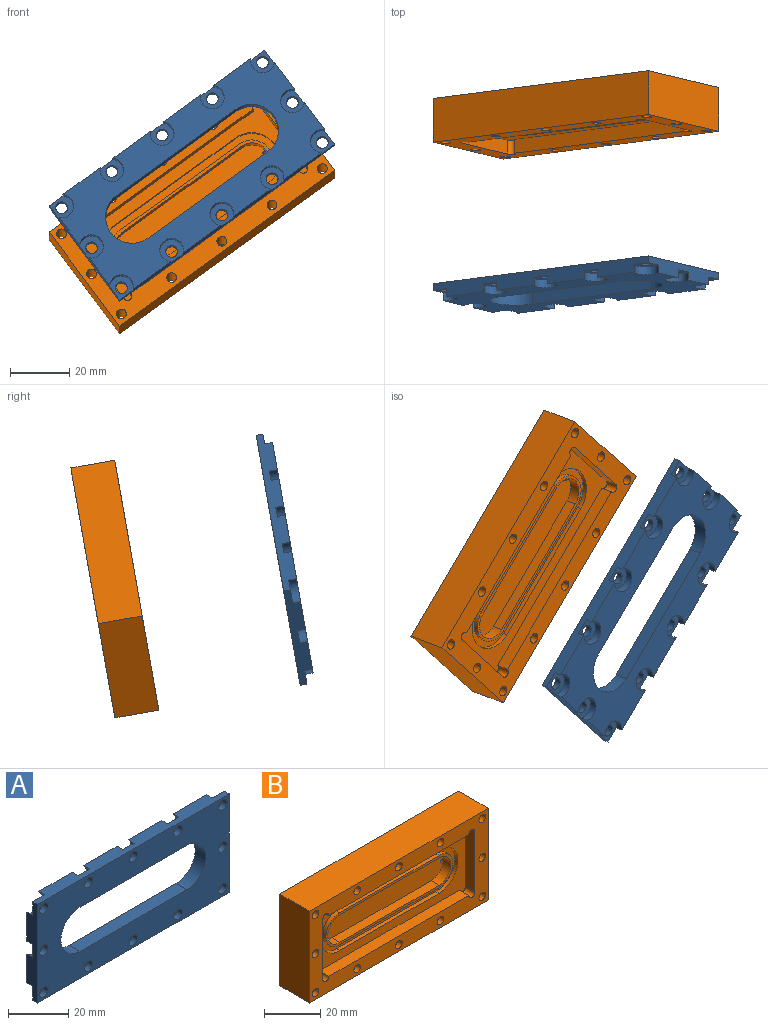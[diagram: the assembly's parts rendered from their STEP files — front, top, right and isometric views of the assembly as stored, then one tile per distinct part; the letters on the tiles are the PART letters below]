
ASSEMBLY  parts=2 mates=2
PART A: 46 faces, bbox 90x5x40 mm
  f0: plane 90x40mm, normal (0,1,0), area 1900.1mm2, adj f2,f3,f4,f17,f18,f20,f22,f24
  f1: plane 90x40mm, normal (0,-1,0), area 2294.7mm2, adj f2,f3,f4,f5,f6,f7,f8,f9
  f2: plane 40x5mm, normal (1,0,0), area 155.2mm2, adj f0,f1,f4,f17,f36,f37,f38,f39
  f3: plane 40x5mm, normal (-1,0,0), area 155.2mm2, adj f0,f1,f4,f17,f24,f25,f26,f27
  f4: plane 90x5mm, normal (0,0,-1), area 376.7mm2, adj f0,f1,f2,f3,f28,f29,f30,f31
  f5: cylinder r=2mm len=4mm, axis (0,1,0), area 28.9mm2, adj f1,f41
  f6: cylinder r=2mm len=4mm, axis (0,1,0), area 28.9mm2, adj f1,f39
  f7: cylinder r=2mm len=4mm, axis (0,1,0), area 28.9mm2, adj f1,f37
  f8: cylinder r=2mm len=4mm, axis (0,1,0), area 28.9mm2, adj f1,f35
  f9: cylinder r=2mm len=4mm, axis (0,1,0), area 28.9mm2, adj f1,f33
  f10: cylinder r=2mm len=4mm, axis (0,1,0), area 28.9mm2, adj f1,f31
  f11: cylinder r=2mm len=4mm, axis (0,1,0), area 28.9mm2, adj f1,f29
  f12: cylinder r=2mm len=4mm, axis (0,1,0), area 28.9mm2, adj f1,f27
  f13: cylinder r=2mm len=4mm, axis (0,1,0), area 28.9mm2, adj f1,f25
  f14: cylinder r=2mm len=4mm, axis (0,1,0), area 28.9mm2, adj f1,f23
  f15: cylinder r=2mm len=4mm, axis (0,1,0), area 28.9mm2, adj f1,f21
  f16: cylinder r=2mm len=4mm, axis (0,1,0), area 28.9mm2, adj f1,f19
  f17: plane 90x5mm, normal (0,0,1), area 376.7mm2, adj f0,f1,f2,f3,f18,f19,f20,f21
  f18: cylinder r=4mm len=8mm, axis (0,1,0), area 52.2mm2, adj f0,f17,f19
  f19: plane 8x7mm, normal (0,1,0), area 34.1mm2, adj f16,f17,f18
  f20: cylinder r=4mm len=8mm, axis (0,1,0), area 52.2mm2, adj f0,f17,f21
  f21: plane 8x7mm, normal (0,1,0), area 34.1mm2, adj f15,f17,f20
  f22: cylinder r=4mm len=8mm, axis (0,1,0), area 52.2mm2, adj f0,f17,f23
  f23: plane 8x7mm, normal (0,1,0), area 34.1mm2, adj f14,f17,f22
  f24: cylinder r=4mm len=7mm, axis (0,1,0), area 35.3mm2, adj f0,f3,f17,f25
  f25: plane 7x7mm, normal (0,1,0), area 30.5mm2, adj f3,f13,f17,f24
  f26: cylinder r=4mm len=8mm, axis (0,1,0), area 52.2mm2, adj f0,f3,f27
  f27: plane 8x7mm, normal (0,1,0), area 34.1mm2, adj f3,f12,f26
  f28: cylinder r=4mm len=7mm, axis (0,1,0), area 35.3mm2, adj f0,f3,f4,f29
  f29: plane 7x7mm, normal (0,1,0), area 30.5mm2, adj f3,f4,f11,f28
  f30: cylinder r=4mm len=8mm, axis (0,1,0), area 52.2mm2, adj f0,f4,f31
  f31: plane 8x7mm, normal (0,1,0), area 34.1mm2, adj f4,f10,f30
  f32: cylinder r=4mm len=8mm, axis (0,1,0), area 52.2mm2, adj f0,f4,f33
  f33: plane 8x7mm, normal (0,1,0), area 34.1mm2, adj f4,f9,f32
  f34: cylinder r=4mm len=8mm, axis (0,1,0), area 52.2mm2, adj f0,f4,f35
  f35: plane 8x7mm, normal (0,1,0), area 34.1mm2, adj f4,f8,f34
  f36: cylinder r=4mm len=7mm, axis (0,1,0), area 35.3mm2, adj f0,f2,f4,f37
  f37: plane 7x7mm, normal (0,1,0), area 30.5mm2, adj f2,f4,f7,f36
  f38: cylinder r=4mm len=8mm, axis (0,1,0), area 52.2mm2, adj f0,f2,f39
  f39: plane 8x7mm, normal (0,1,0), area 34.1mm2, adj f2,f6,f38
  f40: cylinder r=4mm len=7mm, axis (0,1,0), area 35.3mm2, adj f0,f2,f17,f41
  f41: plane 7x7mm, normal (0,1,0), area 30.5mm2, adj f2,f5,f17,f40
  f42: cylinder r=9mm len=18mm, axis (0,-1,0), area 141.4mm2, adj f0,f1,f43,f44
  f43: plane 50x5mm, normal (0,0,-1), area 250mm2, adj f0,f1,f42,f45
  f44: plane 50x5mm, normal (0,0,1), area 250mm2, adj f0,f1,f42,f45
  f45: cylinder r=9mm len=18mm, axis (0,-1,0), area 141.4mm2, adj f0,f1,f43,f44
PART B: 46 faces, bbox 90x15x40 mm
  f0: cylinder r=0.6mm len=5.74mm, axis (0,-1,0), area 21.6mm2, adj f4,f45
  f1: cylinder r=0.6mm len=5.74mm, axis (0,-1,0), area 21.6mm2, adj f4,f44
  f2: plane 90x40mm, normal (0,1,0), area 3489.8mm2, adj f7,f8,f9,f10,f32,f33,f34,f35
  f3: plane 90x40mm, normal (0,-1,0), area 1456mm2, adj f7,f8,f9,f10,f11,f12,f13,f14
  f4: plane 62x12mm, normal (0,-1,0), area 710.8mm2, adj f0,f1,f28,f29,f30,f31
  f5: plane 64x14mm, normal (0,-1,0), area 140.8mm2, adj f22,f23,f24,f25,f28,f29,f30,f31
  f6: plane 76.5x29.5mm, normal (0,-1,0), area 807.9mm2, adj f11,f12,f13,f14,f15,f16,f17,f18
  f7: plane 40x15mm, normal (1,0,0), area 600mm2, adj f2,f3,f8,f10
  f8: plane 90x15mm, normal (0,0,1), area 1350mm2, adj f2,f3,f7,f9
  f9: plane 40x15mm, normal (-1,0,0), area 600mm2, adj f2,f3,f8,f10
  f10: plane 90x15mm, normal (0,0,-1), area 1350mm2, adj f2,f3,f7,f9
  f11: cylinder r=1.5mm len=4.76mm, axis (0,-1,0), area 22.4mm2, adj f3,f6,f12,f18
  f12: plane 70.5x4.76mm, normal (0,0,-1), area 335.6mm2, adj f3,f6,f11,f13
  f13: cylinder r=1.5mm len=4.76mm, axis (0,-1,0), area 22.4mm2, adj f3,f6,f12,f14
  f14: plane 26.5x4.76mm, normal (1,0,0), area 126.1mm2, adj f3,f6,f13,f15
  f15: cylinder r=1.5mm len=4.76mm, axis (0,-1,0), area 22.4mm2, adj f3,f6,f14,f16
  f16: plane 70.5x4.76mm, normal (0,0,1), area 335.6mm2, adj f3,f6,f15,f17
  f17: cylinder r=1.5mm len=4.76mm, axis (0,-1,0), area 22.4mm2, adj f3,f6,f16,f18
  f18: plane 26.5x4.76mm, normal (-1,0,0), area 126.1mm2, adj f3,f6,f11,f17
  f19: plane 50x1.6mm, normal (0,0,-1), area 80mm2, adj f6,f20,f26,f27
  f20: cylinder r=9.5mm len=19mm, axis (0,-1,0), area 47.8mm2, adj f6,f19,f21,f27
  f21: plane 50x1.6mm, normal (0,0,1), area 80mm2, adj f6,f20,f26,f27
  f22: cylinder r=7mm len=14mm, axis (0,-1,0), area 35.2mm2, adj f5,f23,f25,f27
  f23: plane 50x1.6mm, normal (0,0,1), area 80mm2, adj f5,f22,f24,f27
  f24: cylinder r=7mm len=14mm, axis (0,-1,0), area 35.2mm2, adj f5,f23,f25,f27
  f25: plane 50x1.6mm, normal (0,0,-1), area 80mm2, adj f5,f22,f24,f27
  f26: cylinder r=9.5mm len=19mm, axis (0,-1,0), area 47.8mm2, adj f6,f19,f21,f27
  f27: plane 69x19mm, normal (0,-1,0), area 379.6mm2, adj f19,f20,f21,f22,f23,f24,f25,f26
  f28: plane 50x4mm, normal (0,0,-1), area 200mm2, adj f4,f5,f29,f31
  f29: cylinder r=6mm len=12mm, axis (0,-1,0), area 75.4mm2, adj f4,f5,f28,f30
  f30: plane 50x4mm, normal (0,0,1), area 200mm2, adj f4,f5,f29,f31
  f31: cylinder r=6mm len=12mm, axis (0,-1,0), area 75.4mm2, adj f4,f5,f28,f30
  f32: cylinder r=1.65mm len=15mm, axis (0,-1,0), area 155.5mm2, adj f2,f3
  f33: cylinder r=1.65mm len=15mm, axis (0,-1,0), area 155.5mm2, adj f2,f3
  f34: cylinder r=1.65mm len=15mm, axis (0,-1,0), area 155.5mm2, adj f2,f3
  f35: cylinder r=1.65mm len=15mm, axis (0,-1,0), area 155.5mm2, adj f2,f3
  f36: cylinder r=1.65mm len=15mm, axis (0,-1,0), area 155.5mm2, adj f2,f3
  f37: cylinder r=1.65mm len=15mm, axis (0,-1,0), area 155.5mm2, adj f2,f3
  f38: cylinder r=1.65mm len=15mm, axis (0,-1,0), area 155.5mm2, adj f2,f3
  f39: cylinder r=1.65mm len=15mm, axis (0,-1,0), area 155.5mm2, adj f2,f3
  f40: cylinder r=1.65mm len=15mm, axis (0,-1,0), area 155.5mm2, adj f2,f3
  f41: cylinder r=1.65mm len=15mm, axis (0,-1,0), area 155.5mm2, adj f2,f3
  f42: cylinder r=1.65mm len=15mm, axis (0,-1,0), area 155.5mm2, adj f2,f3
  f43: cylinder r=1.65mm len=15mm, axis (0,-1,0), area 155.5mm2, adj f2,f3
  f44: cone r=0.6mm half-angle=45deg, axis (0,1,0), area 3.8mm2, adj f1,f2
  f45: cone r=0.6mm half-angle=45deg, axis (0,1,0), area 3.8mm2, adj f0,f2
PLACE A rot(axis=(0.95,0.03,0.31),170.5deg) t=(-25.06,-84.72,-33.18)mm
PLACE B rot(axis=(-0.03,1,-0.09),143.8deg) t=(-25.06,-32.13,-42.45)mm
MATE planar A.f4 <-> B.f10  axis (-0.59,0.14,0.79) through (-11.51,-78.68,1.06)mm
MATE planar A.f3 <-> B.f7  axis (-0.81,-0.1,-0.58) through (-61.33,-86.55,-59.9)mm
